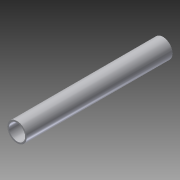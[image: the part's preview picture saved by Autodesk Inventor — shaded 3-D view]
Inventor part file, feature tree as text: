
AUTODESK INVENTOR PART (.ipt)
format: ipt  version: 2015 (Build 190159000, 159)  size: 77,824 bytes
history: native  units: in
note: dims shown in document units (in); Inventor stores cm internally (conversion verified against a paired STEP export)
features: extrude x1, sketch x1
ambient origin geometry x8: Origin, YZ Plane, XZ Plane, XY Plane, X Axis, Y Axis, Z Axis, Center Point
bodies: Solid1 (feature_tree)
feature tree (2):
  extrude  "Extrusion1"  Depth=18.0in
  sketch  "Sketch1"  dims[d0=2.0in d1=2.375in d2=18.0in d3=0.0in]
